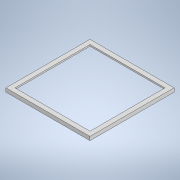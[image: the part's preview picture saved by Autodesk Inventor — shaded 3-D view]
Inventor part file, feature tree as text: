
AUTODESK INVENTOR PART (.ipt)
format: ipt  version: 2020.2 (Build 242310000, 310)  size: 121,856 bytes
history: native  units: mm
features: extrude x2, sketch x2, projected_geometry x1
ambient origin geometry x8: Origin, YZ Plane, XZ Plane, XY Plane, X Axis, Y Axis, Z Axis, Center Point
bodies: Solid1 (feature_tree)
feature tree (5):
  extrude  "Extrusion1"  Depth=0.1mm
  extrude  "Extrusion2"  Depth=4.0mm
  sketch  "Sketch1"  dims[d0=108.004mm d1=0.1mm]
  sketch  "Sketch2"  dims[d2=2.0mm d3=4.0mm d4=2.0mm d5=0.0mm d6=4.0mm d7=3.0mm d8=0.0mm]
  projected_geometry  "Projected Loop1"
